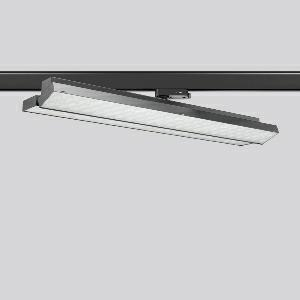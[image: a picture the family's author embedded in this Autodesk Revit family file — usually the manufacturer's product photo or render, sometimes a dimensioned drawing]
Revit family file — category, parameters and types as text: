
# Revit family: tx-move_742163_003_3_85a4
name_source: partatom
category: Lighting Fixtures
units: mm (PartAtom-declared; Revit-internal decimal feet)

## family parameters
Cut with Voids When Loaded = No
Host = Face
Light Source = No
Part Type = Normal
Room Calculation Point = No
Round Connector Dimension = Use Diameter
Shared = No

## types (1)
- MultiLumen 1 (1 x LED Modul 835, 2875 lm, 3500)
    Apparent Load = 41 VA
    CIE Flux Codes = 65 90 98 100 100
    Color Rendering = 80
    Color Temperature = 3500
    Default Elevation = 1800 mm
    Description = Series: TX-MOVE
Multifunctional surface-mounted spotlight for area lighting. Very flat design. Housing: sheet steel, powder-coated. Rotation range: 356°. Swivel range: 90°. Consistent alignment possible with visible tilt scale. High-efficiency LED units with optimum light control thanks to clear plastic (PC) lens optics. Spezielle Mikrostrukturen reduzieren Gelbsaum. Asymmetrical light distribution. With multi adaptor for 3-circuit tracks 230 V. Suitable for Track on ceiling. MultiLumen: Luminous flux adjustable in 3 steps. Factory setting is the highest luminous flux. Environmentally friendly and resource-saving due to replaceable and recyclable components. 
Colour: deep black, matt (RAL 9005)
Length: 570 mm
Width: 119 mm
Height: 92 mm
Lamp: LED
Socket: without socket
Colour temperature: 3500K
Colour rendering index (CRI): 80
System power: 41 W
Rated luminous flux: 5750 lm
Luminous efficiency: 140 lm/W
System power 2: 57 W
Rated luminous flux 2: 7750 lm
Luminous efficiency 2: 136 lm/W
System power 3: 73 W
Rated luminous flux 3: 9450 lm
Luminous efficiency 3: 129 lm/W
Control gear: Regulated power supply
Protection class: I
Type of protection: IP 20
    Height = 75 mm
    Lamp = 1 x LED Modul 835
    Lamp Light Flux = 2875 lm
    Lamp count = 1
    Length = 569 mm
    Lifetime = 50000 h
    Luminous efficacy = 140 lm/W
    Manufacturer = RZB
    ModVariant = No
    Model = 742163.003.3
    Mounting Place = Ceiling
    Mounting Type = Rail mounted
    Number of Poles = 1
    OnlyDefault = Yes
    Power Factor = 1
    Product Name = TX-MOVE
    Product group = Track mounted projectors
    ProductGroupID = 301
    Protection Class = Protection class I
    Protection Degree = IP 20
    RLX_Detail_Level = 1
    RLX_Emergency_Light_Flux = 0 lm
    RLX_Emergency_Type = 0
    RLX_Emergency_Type_DB = No
    RlxData = <blob elided: 57625 chars, md5=f0360bd5>
    Socket = socket
    Standby Power = 0 W
    System Light Flux = 5750 lm
    System Power = 41 W
    Type Comments = MultiLumen 1
    Type Image = 742162.003.jpg
    URL = http://relux.com
    VarID = multilumen_1
    Voltage = 230 V
    Voltage Range = 220-240 V
    Weight = 0.00 kg
    Width = 119 mm

## geometry (parser evidence)
native form markers: Blend x4, Sweep x17
no freeform markers — native parametric forms only
